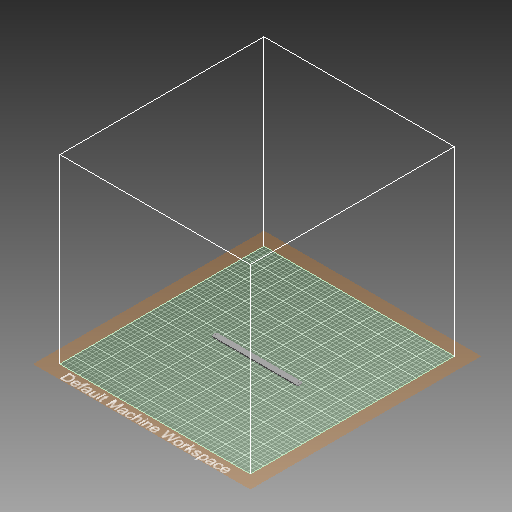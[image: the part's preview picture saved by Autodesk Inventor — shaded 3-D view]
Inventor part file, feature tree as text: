
AUTODESK INVENTOR PART (.ipt)
format: ipt  version: 2019 (Build 230136000, 136)  size: 284,160 bytes
history: native  units: mm (DEFAULTED — no unit token found)
features: extrude x2, sketch x1, projected_geometry x1
ambient origin geometry x8: Origin, YZ Plane, XZ Plane, XY Plane, X Axis, Y Axis, Z Axis, Center Point
bodies: Body1 (feature_tree)
feature tree (4):
  extrude  "Extrusion2"  Depth=2.0mm
  extrude  "Extrusion3"  Depth=2.0mm
  sketch  "Sketch2"  dims[d0=3.0mm d1=3.0mm d2=183.0mm d4=4.0mm d10=2.0mm d11=2.0mm d12=2.0mm d13=2.0mm d14=2.0mm d15=2.0mm d16=2.0mm d17=2.0mm d18=30.0mm d19=9.0mm d20=12.0mm d21=12.0mm d22=12.0mm d23=10.5mm d24=10.5mm d25=9.0mm d26=9.0mm d27=9.0mm d28=9.0mm d29=12.0mm d30=7.6mm d31=0.0mm d32=3.6mm d33=17.5mm d34=2.0mm d35=0.0mm]
  projected_geometry  "Projected Loop1"
